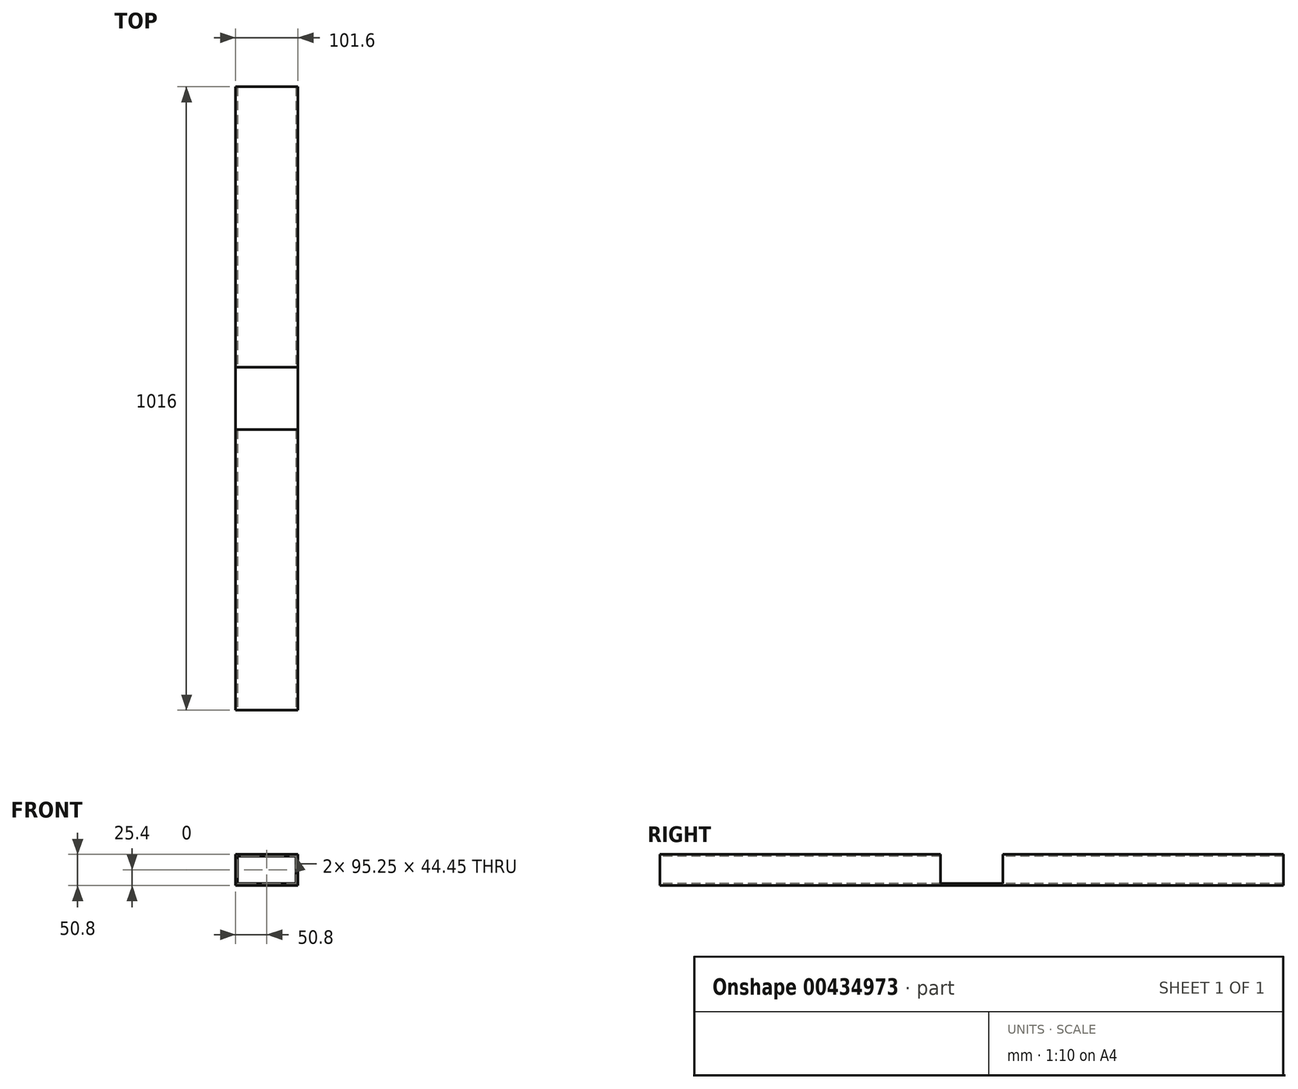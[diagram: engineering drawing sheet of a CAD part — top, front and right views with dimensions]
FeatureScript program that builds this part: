
annotation { "Feature Type Name" : "Feature", "Feature Type Description" : "" }
export const myFeature = defineFeature(function(context is Context, id is Id, definition is map)
    precondition{}
    {
        {
            var Q0;
            Q0=qCreatedBy(makeId("Front.planeOp"),FACE);
            var sketch = newSketch(context, id + "F0", { "sketchPlane" : qUnion([Q0])});
            skLineSegment(sketch, "E0.bottom", {"start": v(0, 0) * mm, "end": v(101.6, 0) * mm});
            skLineSegment(sketch, "E0.top", {"start": v(0, 50.8) * mm, "end": v(101.6, 50.8) * mm});
            skLineSegment(sketch, "E0.left", {"start": v(0, 0) * mm, "end": v(0, 50.8) * mm});
            skLineSegment(sketch, "E0.right", {"start": v(101.6, 0) * mm, "end": v(101.6, 50.8) * mm});
            skLineSegment(sketch, "E1.0", {"start": v(3.17, 3.18) * mm, "end": v(98.43, 3.18) * mm});
            skLineSegment(sketch, "E1.1", {"start": v(3.18, 3.18) * mm, "end": v(3.17, 47.63) * mm});
            skLineSegment(sketch, "E1.2", {"start": v(3.17, 47.63) * mm, "end": v(98.43, 47.63) * mm});
            skLineSegment(sketch, "E1.3", {"start": v(98.43, 3.18) * mm, "end": v(98.43, 47.63) * mm});
            skSolve(sketch);
        }
        {
            var Q0;
            Q0 = qSketchRegion(id + "F0", true);
            extrude(context, id + "F1", {"entities" : qUnion([Q0]), "oppositeDirection" : true, "depth" : 1016 * mm});
        }
        {
            var Q0;
            Q0=qCreatedBy(makeId("Right.planeOp"),FACE);
            var sketch = newSketch(context, id + "F2", { "sketchPlane" : qUnion([Q0])});
            skLineSegment(sketch, "E2.bottom", {"start": v(457.2, 50.8) * mm, "end": v(558.8, 50.8) * mm});
            skLineSegment(sketch, "E2.top", {"start": v(457.2, 3.17) * mm, "end": v(558.8, 3.17) * mm});
            skLineSegment(sketch, "E2.left", {"start": v(457.2, 50.8) * mm, "end": v(457.2, 3.17) * mm});
            skLineSegment(sketch, "E2.right", {"start": v(558.8, 50.8) * mm, "end": v(558.8, 3.18) * mm});
            skPoint(sketch, "E3", {"position": v(508, 50.8) * mm});
            skSolve(sketch);
        }
        {
            var Q0;
            Q0 = qSketchRegion(id + "F2", true);
            extrude(context, id + "F3", {"entities" : qUnion([Q0]), "operationType" : NewBodyOperationType.REMOVE, "endBound" : BoundingType.THROUGH_ALL, "depth" : 25.4 * mm});
        }
    });
